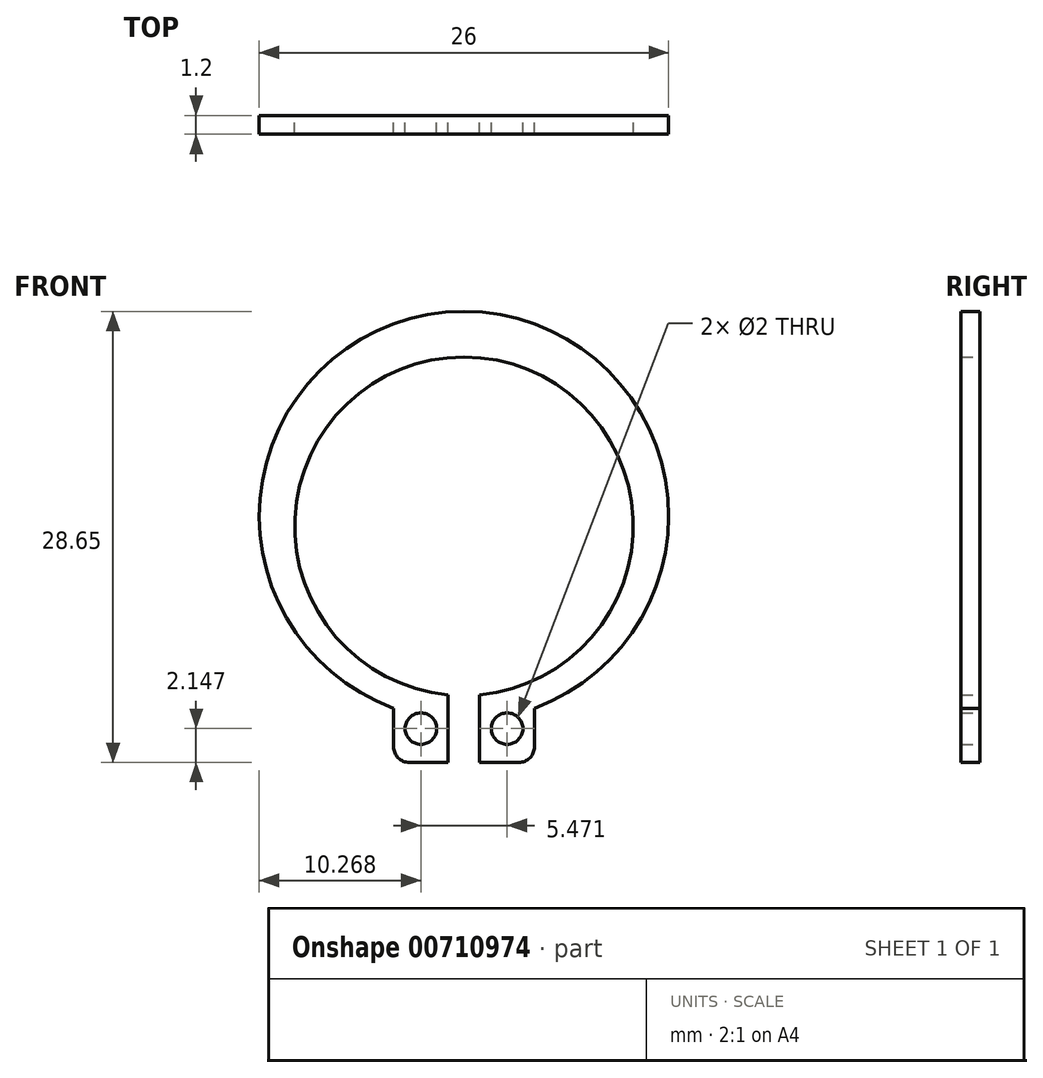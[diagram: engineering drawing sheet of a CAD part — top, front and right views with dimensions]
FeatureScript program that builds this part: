
annotation { "Feature Type Name" : "Feature", "Feature Type Description" : "" }
export const myFeature = defineFeature(function(context is Context, id is Id, definition is map)
    precondition{}
    {
        {
            var Q0;
            Q0=qCreatedBy(makeId("Front.planeOp"),FACE);
            var sketch = newSketch(context, id + "F0", { "sketchPlane" : qUnion([Q0])});
            skCircle(sketch, "E0", {"center": v(33.64, -7.44) * mm, "radius": 10.75 * mm});
            skLineSegment(sketch, "E1", {"start": v(33.64, 11.18) * mm, "end": v(33.64, -28.43) * mm, "construction": true});
            skCircle(sketch, "E2", {"center": v(33.64, -6.79) * mm, "radius": 13 * mm});
            skLineSegment(sketch, "E3.bottom", {"start": v(32.64, -15.66) * mm, "end": v(34.64, -15.66) * mm, "construction": true});
            skLineSegment(sketch, "E3.top", {"start": v(32.64, -22.41) * mm, "end": v(34.64, -22.41) * mm, "construction": true});
            skLineSegment(sketch, "E3.left", {"start": v(32.64, -15.66) * mm, "end": v(32.64, -22.41) * mm, "construction": true});
            skLineSegment(sketch, "E3.right", {"start": v(34.64, -15.66) * mm, "end": v(34.64, -22.41) * mm, "construction": true});
            skPoint(sketch, "E3.middle", {"position": v(33.64, -19.04) * mm});
            skLineSegment(sketch, "E4.bottom", {"start": v(32.64, -18.14) * mm, "end": v(29.17, -18.14) * mm});
            skLineSegment(sketch, "E4.top", {"start": v(32.64, -22.44) * mm, "end": v(30.17, -22.44) * mm});
            skLineSegment(sketch, "E4.left", {"start": v(32.64, -18.14) * mm, "end": v(32.64, -22.44) * mm});
            skLineSegment(sketch, "E4.right", {"start": v(29.17, -18.14) * mm, "end": v(29.17, -21.44) * mm});
            skLineSegment(sketch, "E5.bottom", {"start": v(34.64, -18.14) * mm, "end": v(38.12, -18.14) * mm});
            skLineSegment(sketch, "E5.top", {"start": v(34.64, -22.44) * mm, "end": v(37.12, -22.44) * mm});
            skLineSegment(sketch, "E5.left", {"start": v(34.64, -18.14) * mm, "end": v(34.64, -22.44) * mm});
            skLineSegment(sketch, "E5.right", {"start": v(38.12, -18.14) * mm, "end": v(38.12, -21.44) * mm});
            skLineSegment(sketch, "E6", {"start": v(36.38, -22.44) * mm, "end": v(36.38, -18.14) * mm, "construction": true});
            skLineSegment(sketch, "E7", {"start": v(38.12, -20.3) * mm, "end": v(34.64, -20.3) * mm, "construction": true});
            skCircle(sketch, "E8", {"center": v(36.38, -20.3) * mm, "radius": 1 * mm});
            skLineSegment(sketch, "E9", {"start": v(30.9, -22.44) * mm, "end": v(30.9, -18.14) * mm, "construction": true});
            skLineSegment(sketch, "E10", {"start": v(32.64, -20.3) * mm, "end": v(29.17, -20.3) * mm, "construction": true});
            skCircle(sketch, "E11", {"center": v(30.9, -20.3) * mm, "radius": 1 * mm});
            skPoint(sketch, "E12.visualSharp", {"position": v(29.17, -22.44) * mm});
            skArc(sketch, "E12.filletArc", {"start": v(29.17, -21.44) * mm, "mid": v(29.47, -22.15) * mm, "end": v(30.17, -22.44) * mm});
            skPoint(sketch, "E13.visualSharp", {"position": v(38.12, -22.44) * mm});
            skArc(sketch, "E13.filletArc", {"start": v(37.12, -22.44) * mm, "mid": v(37.82, -22.15) * mm, "end": v(38.12, -21.44) * mm});
            skSolve(sketch);
        }
        {
            var Q0;
            {var subQ0=sQuery(id+"F0.wireOp",EDGE,"E4.bottom");Q0=makeQuery(id+"F0.imprint","IMPRINT",FACE,{"disambiguationData":[TD([[makeQuery(id+"F0.imprint","IMPRINT",EDGE,{"derivedFrom":subQ0}),-1.0]])]});}
            var Q1;
            {var subQ1=sQuery(id+"F0.wireOp",EDGE,"E4.top");Q1=makeQuery(id+"F0.imprint","IMPRINT",FACE,{"disambiguationData":[TD([[makeQuery(id+"F0.imprint","IMPRINT",EDGE,{"derivedFrom":subQ1}),-1.0]])]});}
            var Q2;
            {var subQ0=sQuery(id+"F0.wireOp",EDGE,"E4.bottom");Q2=makeQuery(id+"F0.imprint","IMPRINT",FACE,{"disambiguationData":[TD([[makeQuery(id+"F0.imprint","IMPRINT",EDGE,{"derivedFrom":subQ0}),1.0]])]});}
            var Q3;
            {var subQ1=sQuery(id+"F0.wireOp",EDGE,"E5.bottom");Q3=makeQuery(id+"F0.imprint","IMPRINT",FACE,{"disambiguationData":[TD([[makeQuery(id+"F0.imprint","IMPRINT",EDGE,{"derivedFrom":subQ1}),-1.0]])]});}
            var Q4;
            {var subQ1=sQuery(id+"F0.wireOp",EDGE,"E5.top");Q4=makeQuery(id+"F0.imprint","IMPRINT",FACE,{"disambiguationData":[TD([[makeQuery(id+"F0.imprint","IMPRINT",EDGE,{"derivedFrom":subQ1}),1.0]])]});}
            extrude(context, id + "F1", {"entities" : qUnion([Q0, Q1, Q2, Q3, Q4]), "depth" : 1.2 * mm, "offsetDistance" : 25 * mm});
        }
    });
